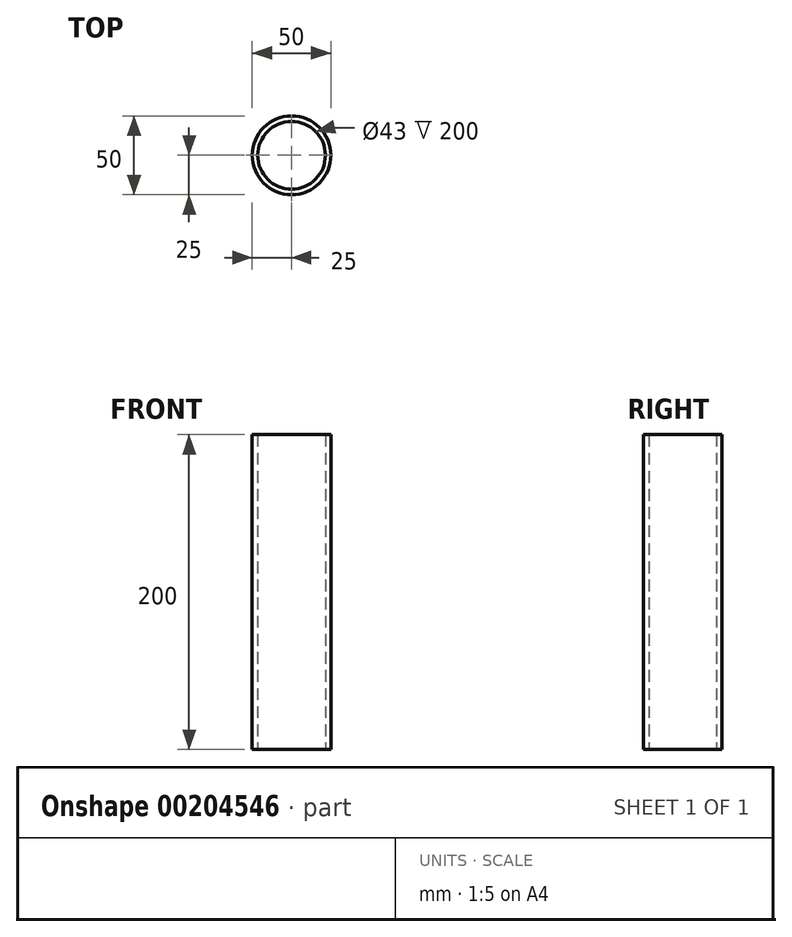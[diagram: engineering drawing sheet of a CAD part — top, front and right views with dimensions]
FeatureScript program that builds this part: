
annotation { "Feature Type Name" : "Feature", "Feature Type Description" : "" }
export const myFeature = defineFeature(function(context is Context, id is Id, definition is map)
    precondition{}
    {
        {
            var Q0;
            Q0=qCreatedBy(makeId("Top.planeOp"),FACE);
            var sketch = newSketch(context, id + "F0", { "sketchPlane" : qUnion([Q0])});
            skCircle(sketch, "E0", {"center": v(0, 0) * mm, "radius": 21.5 * mm});
            skCircle(sketch, "E1", {"center": v(0, 0) * mm, "radius": 25 * mm});
            skSolve(sketch);
        }
        {
            var Q0;
            Q0=makeQuery(id+"F0.imprint","IMPRINT",FACE,{"disambiguationData":[TD([[makeQuery(id+"F0.imprint","IMPRINT",EDGE,{"derivedFrom":sQuery(id+"F0.wireOp",EDGE,"E0")}),-1.0]])]});
            extrude(context, id + "F1", {"entities" : qUnion([Q0]), "depth" : 200 * mm});
        }
    });
